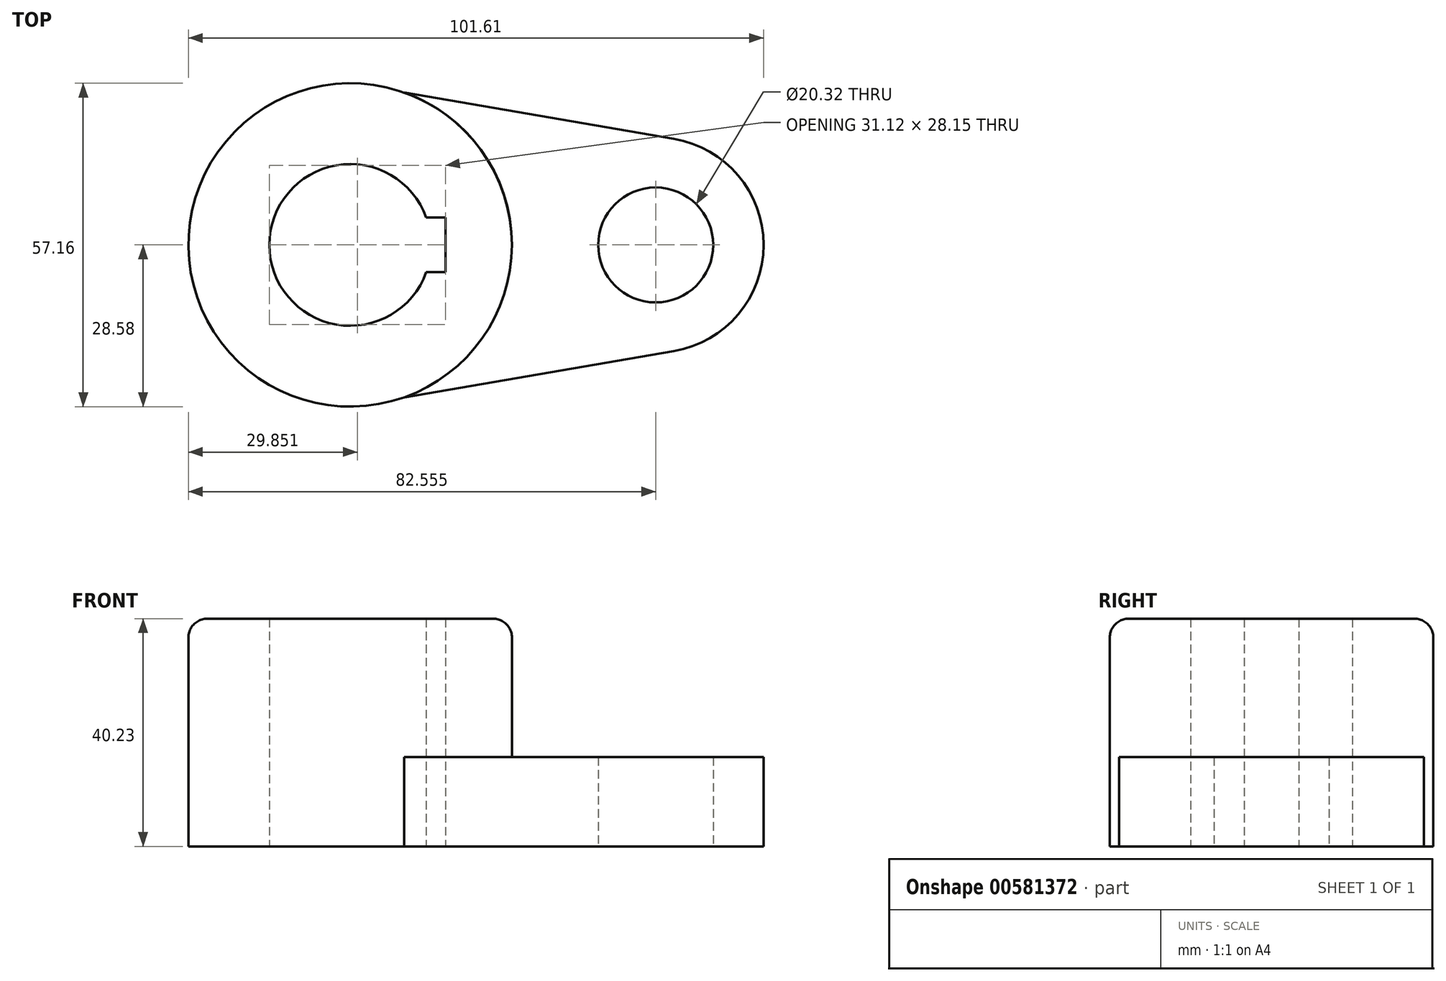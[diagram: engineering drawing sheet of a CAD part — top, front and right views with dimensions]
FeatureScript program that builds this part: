
annotation { "Feature Type Name" : "Feature", "Feature Type Description" : "" }
export const myFeature = defineFeature(function(context is Context, id is Id, definition is map)
    precondition{}
    {
        {
            var Q0;
            Q0=qCreatedBy(makeId("Top.planeOp"),FACE);
            var sketch = newSketch(context, id + "F0", { "sketchPlane" : qUnion([Q0])});
            skCircle(sketch, "E0", {"center": v(0, 0) * mm, "radius": 14.29 * mm});
            skCircle(sketch, "E1", {"center": v(0, 0) * mm, "radius": 28.58 * mm});
            skLineSegment(sketch, "E2.bottom", {"start": v(-13.45, -4.83) * mm, "end": v(16.83, -4.83) * mm});
            skLineSegment(sketch, "E2.top", {"start": v(-13.45, 4.83) * mm, "end": v(16.83, 4.83) * mm});
            skLineSegment(sketch, "E2.left", {"start": v(-13.45, -4.83) * mm, "end": v(-13.45, 4.83) * mm});
            skLineSegment(sketch, "E2.right", {"start": v(16.83, -4.83) * mm, "end": v(16.83, 4.83) * mm});
            skPoint(sketch, "E2.middle", {"position": v(1.7, 0) * mm});
            skSolve(sketch);
        }
        {
            var Q0;
            Q0=makeQuery(id+"F0.imprint","IMPRINT",FACE,{"disambiguationData":[TD([[makeQuery(id+"F0.imprint","IMPRINT",EDGE,{"derivedFrom":sQuery(id+"F0.wireOp",EDGE,"E0")}),-1.0]])]});
            extrude(context, id + "F1", {"entities" : qUnion([Q0]), "depth" : 40.23 * mm, "offsetDistance" : 25.4 * mm});
        }
        {
            var Q0;
            Q0=qCreatedBy(makeId("Top.planeOp"),FACE);
            var sketch = newSketch(context, id + "F2", { "sketchPlane" : qUnion([Q0])});
            skLineSegment(sketch, "E3", {"start": v(0, 0) * mm, "end": v(53.98, 0) * mm, "construction": true});
            skCircle(sketch, "E4", {"center": v(53.98, 0) * mm, "radius": 10.16 * mm});
            skCircle(sketch, "E5", {"center": v(53.98, 0) * mm, "radius": 19.05 * mm});
            skCircle(sketch, "E6.0", {"center": v(0, 0) * mm, "radius": 28.58 * mm});
            skCircle(sketch, "E7.0", {"center": v(0, 0) * mm, "radius": 14.29 * mm});
            skLineSegment(sketch, "E8", {"start": v(0, 28.57) * mm, "end": v(57.2, 18.78) * mm});
            skLineSegment(sketch, "E9", {"start": v(0, -28.57) * mm, "end": v(57.2, -18.78) * mm});
            skSolve(sketch);
        }
        {
            var Q0;
            {var subQ0=sQuery(id+"F2.wireOp",EDGE,"E8");var subQ1=sQuery(id+"F2.wireOp",EDGE,"E5");var subQ2=makeQuery(id+"F2.imprint","INTERSECT",VERTEX,{"derivedFrom":[subQ1,subQ0]});Q0=makeQuery(id+"F2.imprint","IMPRINT",FACE,{"disambiguationData":[TD([[makeQuery(id+"F2.imprint","IMPRINT",EDGE,{"disambiguationData":[TD([[subQ2,-1.0]])],"derivedFrom":subQ1}),-1.0]])]});}
            var Q1;
            Q1=makeQuery(id+"F2.imprint","IMPRINT",FACE,{"disambiguationData":[TD([[makeQuery(id+"F2.imprint","IMPRINT",EDGE,{"derivedFrom":sQuery(id+"F2.wireOp",EDGE,"E4")}),-1.0]])]});
            extrude(context, id + "F3", {"entities" : qUnion([Q0, Q1]), "operationType" : NewBodyOperationType.ADD, "depth" : 15.77 * mm, "offsetDistance" : 25.4 * mm});
        }
        {
            var Q0;
            Q0 = qSketchRegion(id + "F0", true);
            extrude(context, id + "F4", {"entities" : qUnion([Q0]), "operationType" : NewBodyOperationType.ADD, "depth" : 25.4 * mm, "offsetDistance" : 25.4 * mm});
        }
        {
            var Q0;
            Q0=makeQuery(id+"F1.opExtrude","CAP_EDGE",EDGE,{"disambiguationData":[OSD([sQuery(id+"F0.wireOp",EDGE,"E1")])],"isStart":false});
            fillet(context, id + "F5", {"entities" : qUnion([Q0]), "radius" : 3.3 * mm, "tangentPropagation" : true, "allowEdgeOverflow" : false});
        }
    });
